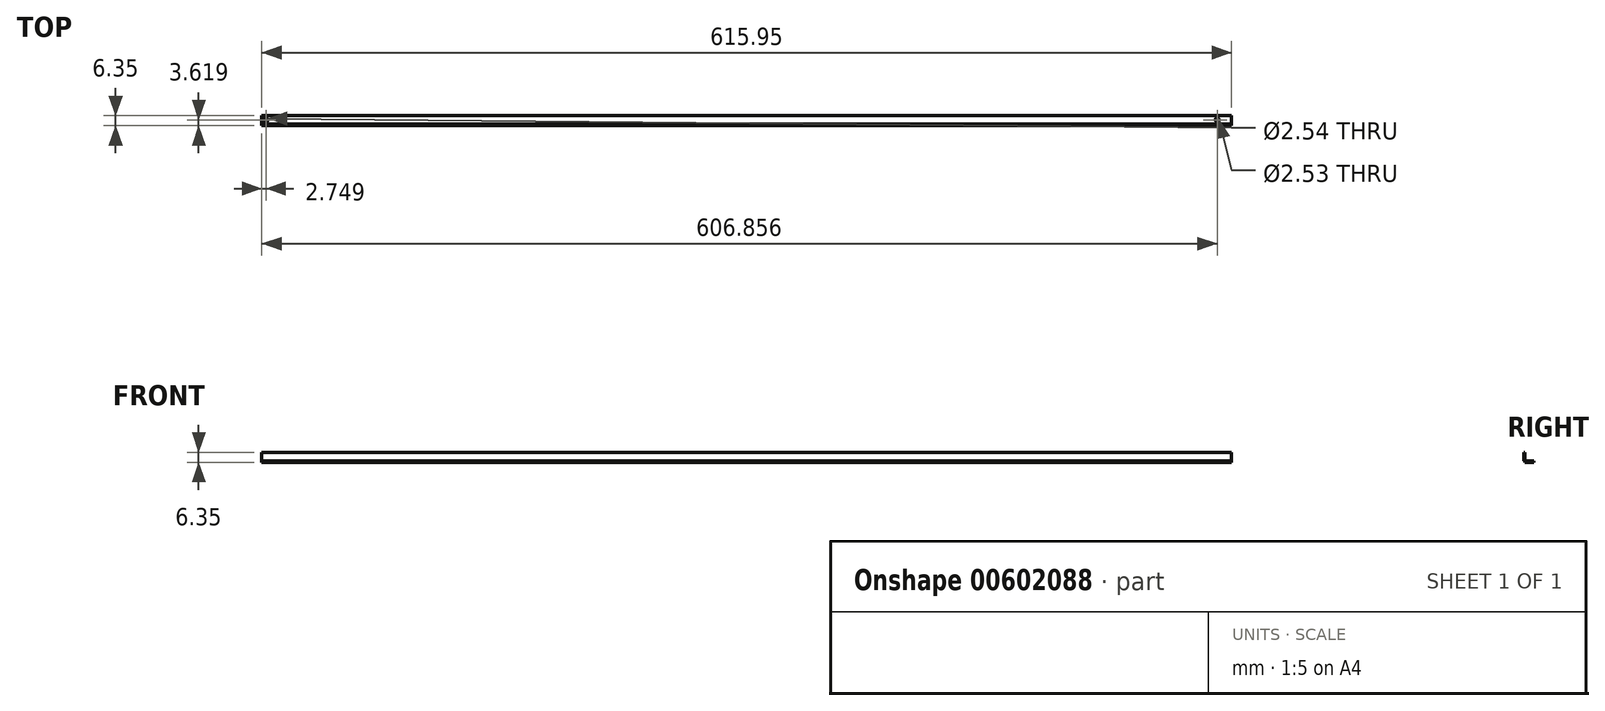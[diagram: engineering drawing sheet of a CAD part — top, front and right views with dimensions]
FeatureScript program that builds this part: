
annotation { "Feature Type Name" : "Feature", "Feature Type Description" : "" }
export const myFeature = defineFeature(function(context is Context, id is Id, definition is map)
    precondition{}
    {
        {
            var Q0;
            Q0=qCreatedBy(makeId("Right.planeOp"),FACE);
            var sketch = newSketch(context, id + "F0", { "sketchPlane" : qUnion([Q0])});
            skLineSegment(sketch, "E0.bottom", {"start": v(0, 0) * mm, "end": v(0.89, 0) * mm});
            skLineSegment(sketch, "E0.top", {"start": v(0, 6.35) * mm, "end": v(0.89, 6.35) * mm});
            skLineSegment(sketch, "E0.left", {"start": v(0, 0) * mm, "end": v(0, 6.35) * mm});
            skLineSegment(sketch, "E0.right", {"start": v(0.89, 0) * mm, "end": v(0.89, 6.35) * mm});
            skLineSegment(sketch, "E1.bottom", {"start": v(0, 0) * mm, "end": v(6.35, 0) * mm});
            skLineSegment(sketch, "E1.top", {"start": v(0, 0.89) * mm, "end": v(6.35, 0.89) * mm});
            skLineSegment(sketch, "E1.left", {"start": v(0, 0) * mm, "end": v(0, 0.89) * mm});
            skLineSegment(sketch, "E1.right", {"start": v(6.35, 0) * mm, "end": v(6.35, 0.89) * mm});
            skSolve(sketch);
        }
        {
            var Q0;
            {var subQ0=sQuery(id+"F0.wireOp",EDGE,"E0.top");Q0=makeQuery(id+"F0.imprint","IMPRINT",FACE,{"disambiguationData":[TD([[makeQuery(id+"F0.imprint","IMPRINT",EDGE,{"derivedFrom":subQ0}),-1.0]])]});}
            var Q1;
            {var subQ5=sQuery(id+"F0.wireOp",EDGE,"E1.right");Q1=makeQuery(id+"F0.imprint","IMPRINT",FACE,{"disambiguationData":[TD([[makeQuery(id+"F0.imprint","IMPRINT",EDGE,{"derivedFrom":subQ5}),1.0]])]});}
            var Q2;
            {var subQ5=sQuery(id+"F0.wireOp",EDGE,"E1.left");Q2=makeQuery(id+"F0.imprint","IMPRINT",FACE,{"disambiguationData":[TD([[makeQuery(id+"F0.imprint","IMPRINT",EDGE,{"derivedFrom":subQ5}),-1.0]])]});}
            extrude(context, id + "F1", {"entities" : qUnion([Q0, Q1, Q2]), "depth" : 615.95 * mm, "offsetDistance" : 25.4 * mm});
        }
        {
            var Q0;
            Q0=makeQuery(id+"F1.opExtrude","SWEPT_FACE",FACE,{"disambiguationData":[OSD([sQuery(id+"F0.wireOp",EDGE,"E1.top")])]});
            var sketch = newSketch(context, id + "F2", { "sketchPlane" : qUnion([Q0])});
            skLineSegment(sketch, "E2", {"start": v(0, 0.89) * mm, "end": v(2.75, 0.89) * mm});
            skCircle(sketch, "E3", {"center": v(2.75, 3.62) * mm, "radius": 1.27 * mm});
            skPoint(sketch, "E3.centerSnap0", {"position": v(0, 3.62) * mm});
            skLineSegment(sketch, "E4", {"start": v(615.95, 0.89) * mm, "end": v(606.86, 0.89) * mm});
            skCircle(sketch, "E5", {"center": v(606.86, 3.62) * mm, "radius": 1.27 * mm});
            skPoint(sketch, "E5.centerSnap0", {"position": v(615.95, 3.62) * mm});
            skSolve(sketch);
        }
        {
            var Q0;
            Q0=makeQuery(id+"F2.imprint","IMPRINT",FACE,{"disambiguationData":[TD([[makeQuery(id+"F2.imprint","IMPRINT",EDGE,{"derivedFrom":sQuery(id+"F2.wireOp",EDGE,"E5")}),1.0]])]});
            var Q1;
            Q1=makeQuery(id+"F2.imprint","IMPRINT",FACE,{"disambiguationData":[TD([[makeQuery(id+"F2.imprint","IMPRINT",EDGE,{"derivedFrom":sQuery(id+"F2.wireOp",EDGE,"E3")}),1.0]])]});
            extrude(context, id + "F3", {"entities" : qUnion([Q0, Q1]), "operationType" : NewBodyOperationType.REMOVE, "oppositeDirection" : true, "depth" : 25.4 * mm, "offsetDistance" : 25.4 * mm});
        }
    });
